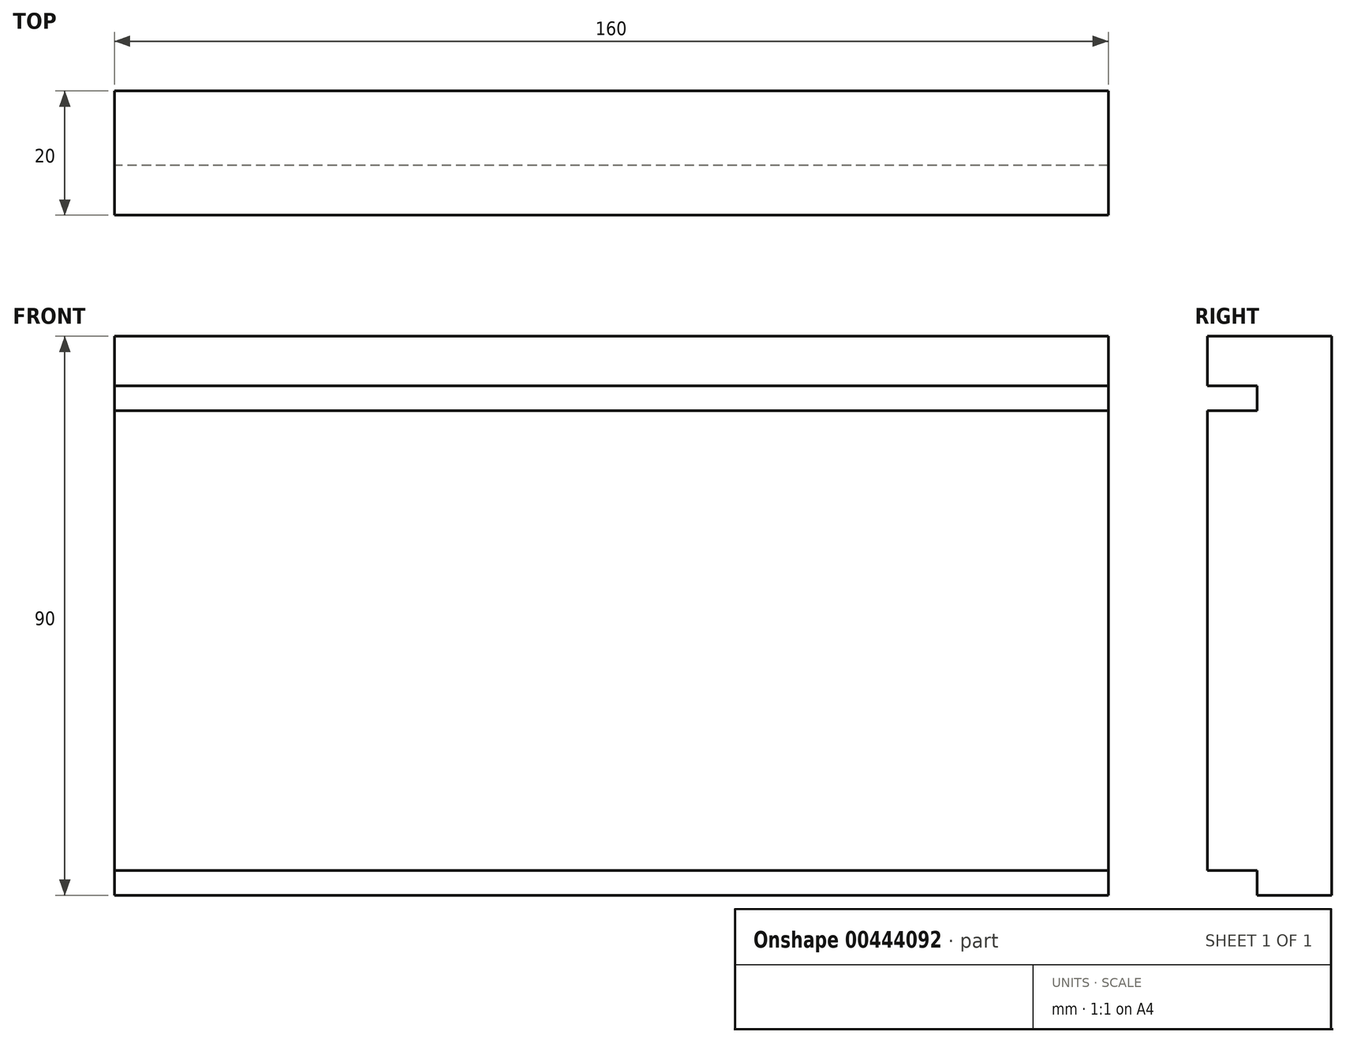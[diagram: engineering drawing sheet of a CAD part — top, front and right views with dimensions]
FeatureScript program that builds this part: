
annotation { "Feature Type Name" : "Feature", "Feature Type Description" : "" }
export const myFeature = defineFeature(function(context is Context, id is Id, definition is map)
    precondition{}
    {
        {
            var Q0;
            Q0=qCreatedBy(makeId("Right.planeOp"),FACE);
            var sketch = newSketch(context, id + "F0", { "sketchPlane" : qUnion([Q0])});
            skLineSegment(sketch, "E0", {"start": v(-42.7, 50.4) * mm, "end": v(-22.7, 50.4) * mm});
            skLineSegment(sketch, "E1", {"start": v(-22.7, 50.4) * mm, "end": v(-22.7, -39.6) * mm});
            skLineSegment(sketch, "E2", {"start": v(-22.7, -39.6) * mm, "end": v(-34.7, -39.6) * mm});
            skLineSegment(sketch, "E3", {"start": v(-34.7, -39.6) * mm, "end": v(-34.7, -35.6) * mm});
            skLineSegment(sketch, "E4", {"start": v(-34.7, -35.6) * mm, "end": v(-42.7, -35.6) * mm});
            skLineSegment(sketch, "E5", {"start": v(-42.7, -35.6) * mm, "end": v(-42.7, 38.4) * mm});
            skLineSegment(sketch, "E6", {"start": v(-42.7, 38.4) * mm, "end": v(-34.7, 38.4) * mm});
            skLineSegment(sketch, "E7", {"start": v(-34.7, 38.4) * mm, "end": v(-34.7, 42.4) * mm});
            skLineSegment(sketch, "E8", {"start": v(-34.7, 42.4) * mm, "end": v(-42.7, 42.4) * mm});
            skLineSegment(sketch, "E9", {"start": v(-42.7, 42.4) * mm, "end": v(-42.7, 50.4) * mm});
            skSolve(sketch);
        }
        {
            var Q0;
            Q0 = qSketchRegion(id + "F0", true);
            extrude(context, id + "F1", {"entities" : qUnion([Q0]), "depth" : 160 * mm});
        }
    });
